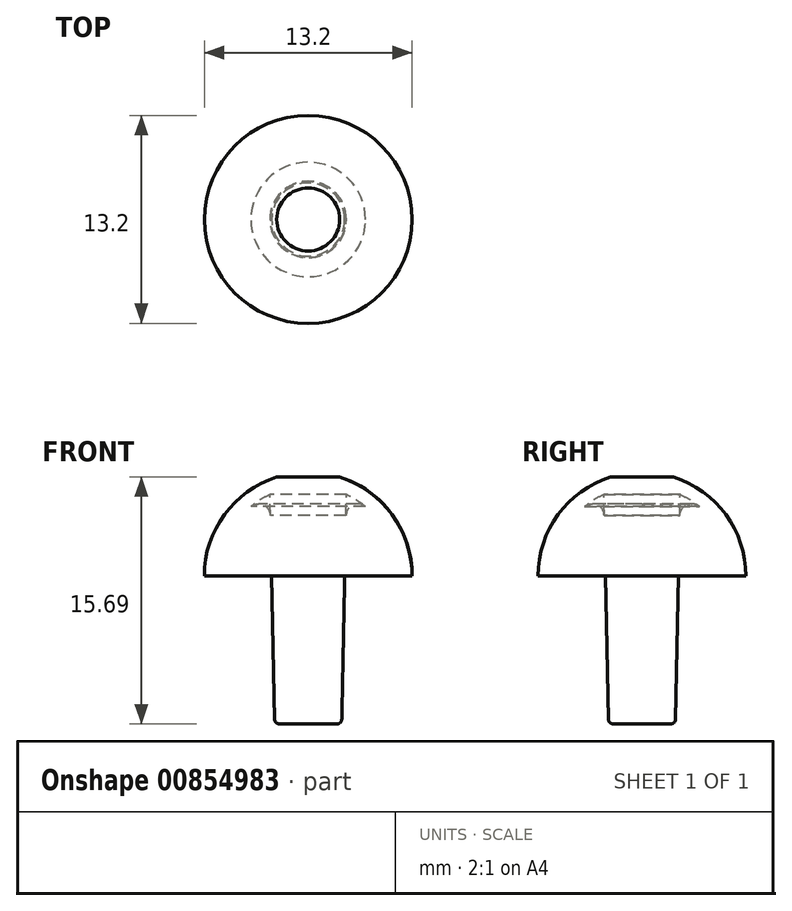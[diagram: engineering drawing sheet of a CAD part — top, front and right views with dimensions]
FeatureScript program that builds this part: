
annotation { "Feature Type Name" : "Feature", "Feature Type Description" : "" }
export const myFeature = defineFeature(function(context is Context, id is Id, definition is map)
    precondition{}
    {
        {
            var Q0;
            Q0=qCreatedBy(makeId("Front.planeOp"),FACE);
            var sketch = newSketch(context, id + "F0", { "sketchPlane" : qUnion([Q0])});
            skArc(sketch, "E0", {"start": v(6.6, 0) * mm, "mid": v(5.33, 3.9) * mm, "end": v(2, 6.29) * mm});
            skArc(sketch, "E1", {"start": v(5.7, 0) * mm, "mid": v(4.04, 4.04) * mm, "end": v(0, 5.7) * mm});
            skLineSegment(sketch, "E2", {"start": v(5.7, 0) * mm, "end": v(6.6, 0) * mm});
            skLineSegment(sketch, "E3", {"start": v(0, 6.6) * mm, "end": v(0, -9.4) * mm, "construction": true});
            skLineSegment(sketch, "E4", {"start": v(2.43, 5.17) * mm, "end": v(2.13, -9.1) * mm});
            skLineSegment(sketch, "E5", {"start": v(1.83, -9.4) * mm, "end": v(0, -9.4) * mm});
            skLineSegment(sketch, "E6", {"start": v(0, 5.7) * mm, "end": v(0, -9.4) * mm});
            skPoint(sketch, "E7.visualSharp", {"position": v(2.13, -9.4) * mm});
            skArc(sketch, "E7.filletArc", {"start": v(1.83, -9.4) * mm, "mid": v(2.04, -9.31) * mm, "end": v(2.13, -9.1) * mm});
            skArc(sketch, "E8", {"start": v(3.64, 4.4) * mm, "mid": v(2.84, 4.5) * mm, "end": v(2.4, 3.84) * mm});
            skLineSegment(sketch, "E9", {"start": v(5.7, 0) * mm, "end": v(0.03, 0.03) * mm});
            skLineSegment(sketch, "E10", {"start": v(0, 6.29) * mm, "end": v(2, 6.29) * mm});
            skLineSegment(sketch, "E11", {"start": v(0, 6.29) * mm, "end": v(0, -9.4) * mm});
            skLineSegment(sketch, "E12", {"start": v(0, 6.29) * mm, "end": v(0, 5.7) * mm});
            skSolve(sketch);
        }
        {
            var Q0;
            Q0 = qSketchRegion(id + "F0", true);
            var Q1;
            Q1=sQuery(id+"F0.wireOp",EDGE,"E12");
            revolve(context, id + "F1", {"surfaceOperationType" : NewSurfaceOperationType.NEW, "entities" : qUnion([Q0]), "axis" : qUnion([Q1]), "revolveType" : RevolveType.FULL});
        }
    });
